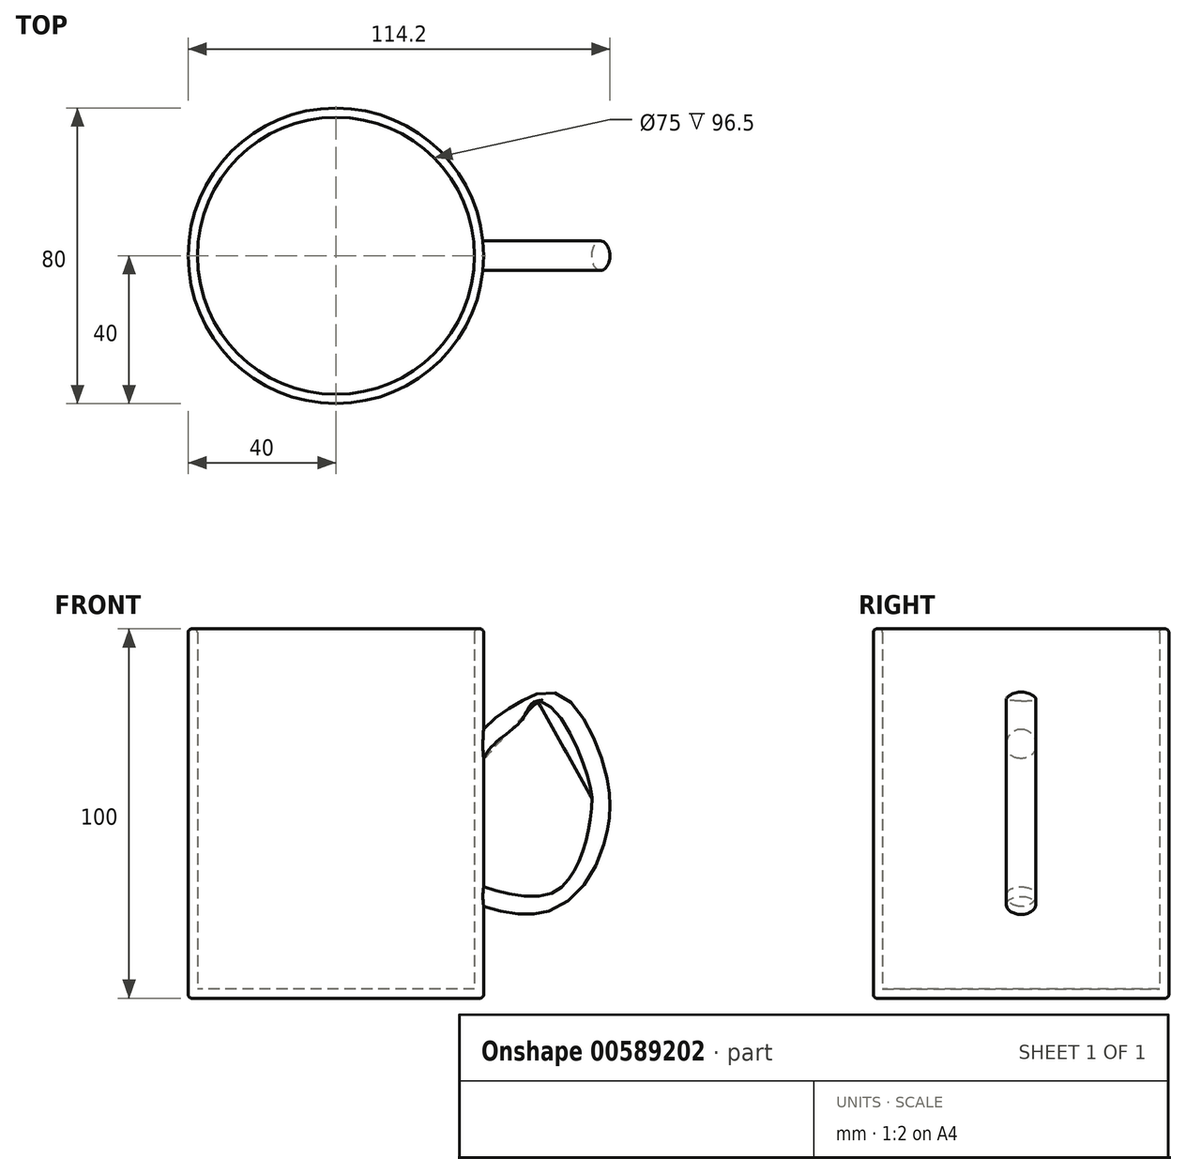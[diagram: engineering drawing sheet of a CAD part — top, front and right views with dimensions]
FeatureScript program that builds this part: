
annotation { "Feature Type Name" : "Feature", "Feature Type Description" : "" }
export const myFeature = defineFeature(function(context is Context, id is Id, definition is map)
    precondition{}
    {
        {
            var Q0;
            Q0=qCreatedBy(makeId("Top.planeOp"),FACE);
            var sketch = newSketch(context, id + "F0", { "sketchPlane" : qUnion([Q0])});
            skCircle(sketch, "E0", {"center": v(0, 0) * mm, "radius": 40 * mm});
            skSolve(sketch);
        }
        {
            var Q0;
            Q0 = qSketchRegion(id + "F0", true);
            extrude(context, id + "F1", {"entities" : qUnion([Q0]), "depth" : 100 * mm, "offsetDistance" : 25 * mm});
        }
        {
            var Q0;
            Q0=qCreatedBy(makeId("Front.planeOp"),FACE);
            var sketch = newSketch(context, id + "F2", { "sketchPlane" : qUnion([Q0])});
            skFitSpline(sketch, "E1", {"points": [v(37.5, 70.02) * mm, v(48.1, 79.49) * mm, v(61.03, 82.34) * mm, v(73.53, 59.97) * mm, v(73.31, 43.53) * mm, v(67.17, 30.15) * mm, v(53.36, 22.48) * mm, v(31.83, 28.07) * mm], "startDerivative": vector(51.55, 87.22) * mm, "endDerivative": vector(-94.72, 52.67) * mm});
            skSolve(sketch);
        }
        {
            var Q0;
            Q0=qCreatedBy(makeId("Right.planeOp"),FACE);
            cPlane(context, id + "F3", {"entities" : qUnion([Q0]), "cplaneType" : CPlaneType.OFFSET, "offset" : 40 * mm, "width" : 150 * mm, "height" : 150 * mm});
        }
        {
            var Q0;
            Q0=qCreatedBy(id+"F3.planeOp",FACE);
            var sketch = newSketch(context, id + "F4", { "sketchPlane" : qUnion([Q0])});
            skCircle(sketch, "E2", {"center": v(0, 68.9) * mm, "radius": 4 * mm});
            skSolve(sketch);
        }
        {
            var Q0;
            Q0=makeQuery(id+"F4.imprint","IMPRINT",FACE,{"disambiguationData":[TD([[makeQuery(id+"F4.imprint","IMPRINT",EDGE,{"derivedFrom":sQuery(id+"F4.wireOp",EDGE,"E2")}),1.0]])]});
            var Q1;
            Q1=sQuery(id+"F2.wireOp",EDGE,"E1");
            sweep(context, id + "F5", {"operationType" : NewBodyOperationType.ADD, "profiles" : qUnion([Q0]), "path" : qUnion([Q1])});
        }
        {
            var Q0;
            Q0=makeQuery(id+"F1.opExtrude","CAP_FACE",FACE,{"disambiguationData":[OSD([sQuery(id+"F0.wireOp",EDGE,"E0")])],"isStart":false});
            shell(context, id + "F6", {"entities" : qUnion([Q0]), "thickness" : 2.5 * mm});
        }
        {
            var Q0;
            Q0=makeQuery(id+"F1.opExtrude","CAP_EDGE",EDGE,{"disambiguationData":[OSD([sQuery(id+"F0.wireOp",EDGE,"E0")])],"isStart":false});
            fillet(context, id + "F7", {"entities" : qUnion([Q0]), "radius" : 1 * mm, "tangentPropagation" : true, "allowEdgeOverflow" : false});
        }
        {
            var Q0;
            {var subQ0=sQuery(id+"F0.wireOp",EDGE,"E0");Q0=makeQuery(id+"F6.opShell","OFFSET_EDGE",EDGE,{"disambiguationData":[OSD([subQ0]),TDD([makeQuery(id+"F1.opExtrude","CAP_EDGE",EDGE,{"disambiguationData":[OSD([subQ0])],"isStart":false})])]});}
            fillet(context, id + "F8", {"entities" : qUnion([Q0]), "radius" : 1 * mm, "tangentPropagation" : true, "allowEdgeOverflow" : false});
        }
        {
            var Q0;
            Q0=makeQuery(id+"F1.opExtrude","CAP_EDGE",EDGE,{"disambiguationData":[OSD([sQuery(id+"F0.wireOp",EDGE,"E0")])],"isStart":true});
            fillet(context, id + "F9", {"entities" : qUnion([Q0]), "radius" : 1 * mm, "tangentPropagation" : true, "allowEdgeOverflow" : false});
        }
    });
